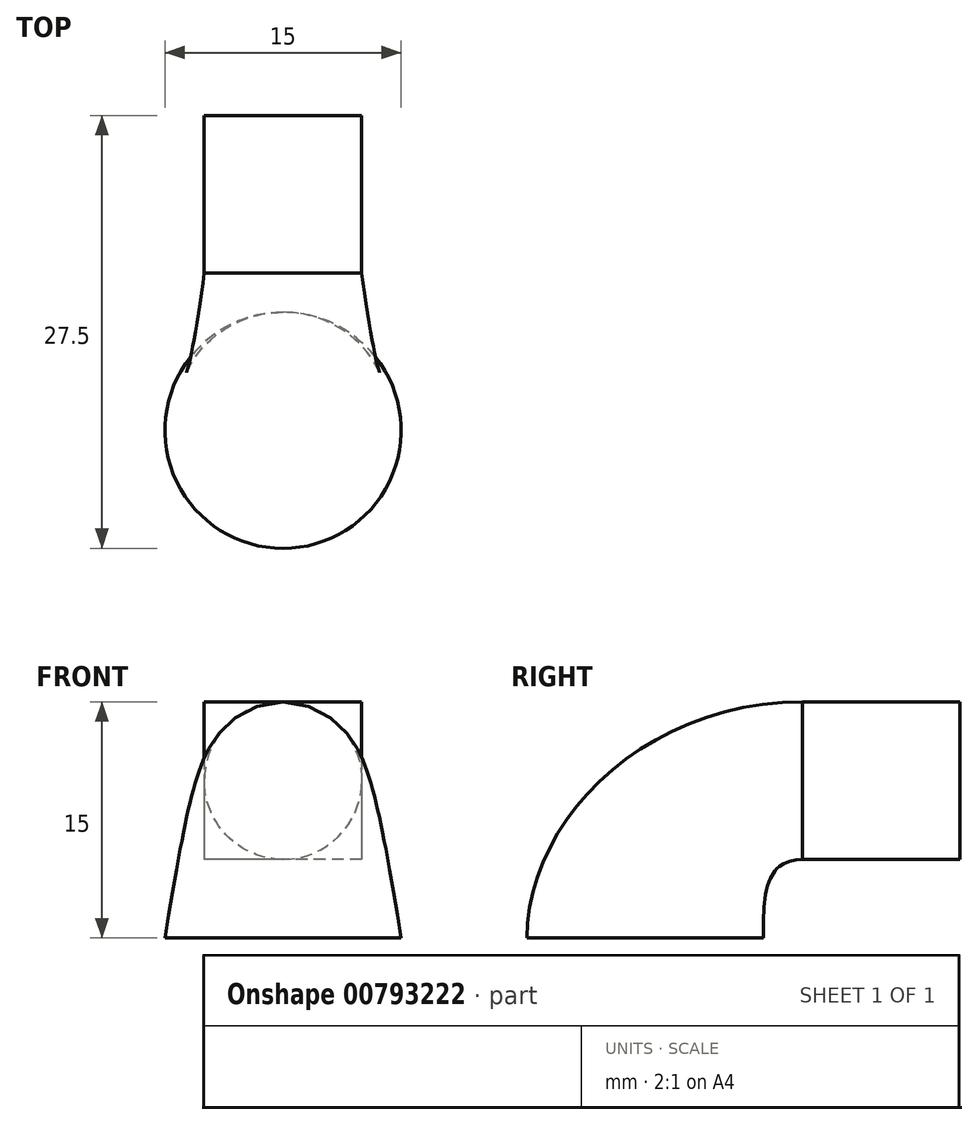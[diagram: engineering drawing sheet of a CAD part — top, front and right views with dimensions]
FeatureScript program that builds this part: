
annotation { "Feature Type Name" : "Feature", "Feature Type Description" : "" }
export const myFeature = defineFeature(function(context is Context, id is Id, definition is map)
    precondition{}
    {
        {
            var Q0;
            Q0=qCreatedBy(makeId("Top.planeOp"),FACE);
            var sketch = newSketch(context, id + "F0", { "sketchPlane" : qUnion([Q0])});
            skPoint(sketch, "E0", {"position": v(0, 0) * mm});
            skLineSegment(sketch, "E1", {"start": v(0, 0) * mm, "end": v(5, 5) * mm, "construction": true});
            skLineSegment(sketch, "E2.bottom", {"start": v(5, 5) * mm, "end": v(-5, 5) * mm});
            skLineSegment(sketch, "E2.top", {"start": v(5, -5) * mm, "end": v(-5, -5) * mm});
            skLineSegment(sketch, "E2.left", {"start": v(5, 5) * mm, "end": v(5, -5) * mm});
            skLineSegment(sketch, "E2.right", {"start": v(-5, 5) * mm, "end": v(-5, -5) * mm});
            skSolve(sketch);
        }
        {
            var Q0;
            Q0=qCreatedBy(makeId("Right.planeOp"),FACE);
            var Q1;
            Q1=sQuery(id+"F0.wireOp",VERTEX,"E1.end");
            cPlane(context, id + "F1", {"entities" : qUnion([Q0, Q1]), "cplaneType" : CPlaneType.PLANE_POINT, "offset" : 0 * mm, "width" : 150 * mm, "height" : 150 * mm});
        }
        {
            var Q0;
            Q0=qCreatedBy(id+"F1.planeOp",FACE);
            var sketch = newSketch(context, id + "F2", { "sketchPlane" : qUnion([Q0])});
            skPoint(sketch, "E3", {"position": v(5, 0) * mm});
            skLineSegment(sketch, "E4", {"start": v(5, 0) * mm, "end": v(5, 10) * mm, "construction": true});
            skSolve(sketch);
        }
        {
            var Q0;
            Q0 = qSketchRegion(id + "F0", true);
            var Q1;
            Q1=sQuery(id+"F2.wireOp",VERTEX,"E4.end");
            extrude(context, id + "F3", {"entities" : qUnion([Q0]), "endBound" : BoundingType.UP_TO_VERTEX, "depth" : 25 * mm, "endBoundEntityVertex" : qUnion([Q1]), "offsetDistance" : 25 * mm});
        }
        {
            var Q0;
            Q0=makeQuery(id+"F3.opExtrude","CAP_FACE",FACE,{"disambiguationData":[OSD([sQuery(id+"F0.wireOp",EDGE,"E2.bottom"),sQuery(id+"F0.wireOp",EDGE,"E2.top"),sQuery(id+"F0.wireOp",EDGE,"E2.left"),sQuery(id+"F0.wireOp",EDGE,"E2.right")])],"isStart":true});
            cPlane(context, id + "F4", {"entities" : qUnion([Q0]), "cplaneType" : CPlaneType.OFFSET, "offset" : 5 * mm, "width" : 150 * mm, "height" : 150 * mm});
        }
        {
            var Q0;
            Q0=makeQuery(id+"F3.opExtrude","SWEPT_FACE",FACE,{"disambiguationData":[OSD([sQuery(id+"F0.wireOp",EDGE,"E2.top")])]});
            var sketch = newSketch(context, id + "F5", { "sketchPlane" : qUnion([Q0])});
            skLineSegment(sketch, "E5", {"start": v(0, 0) * mm, "end": v(0, 5) * mm, "construction": true});
            skCircle(sketch, "E6", {"center": v(0, 5) * mm, "radius": 5 * mm});
            skSolve(sketch);
        }
        {
            var Q0;
            Q0=qCreatedBy(id+"F4.planeOp",FACE);
            var sketch = newSketch(context, id + "F6", { "sketchPlane" : qUnion([Q0])});
            skLineSegment(sketch, "E7", {"start": v(0, 15) * mm, "end": v(0, 5) * mm, "construction": true});
            skCircle(sketch, "E8", {"center": v(0, 15) * mm, "radius": 7.5 * mm});
            skPoint(sketch, "E9", {"position": v(0, 7.5) * mm});
            skPoint(sketch, "E10", {"position": v(0, 22.5) * mm});
            skSolve(sketch);
        }
        {
            var Q0;
            Q0=qCreatedBy(makeId("Right.planeOp"),FACE);
            var Q1;
            Q1=sQuery(id+"F5.wireOp",VERTEX,"E5.end");
            cPlane(context, id + "F7", {"entities" : qUnion([Q0, Q1]), "cplaneType" : CPlaneType.PLANE_POINT, "offset" : 25 * mm, "width" : 150 * mm, "height" : 150 * mm});
        }
        {
            var Q0;
            Q0=qCreatedBy(id+"F7.planeOp",FACE);
            var sketch = newSketch(context, id + "F8", { "sketchPlane" : qUnion([Q0])});
            skLineSegment(sketch, "E11", {"start": v(-5, 0) * mm, "end": v(-4.5, 0) * mm, "construction": true});
            skLineSegment(sketch, "E12", {"start": v(-4.5, 10) * mm, "end": v(-5, 10) * mm, "construction": true});
            skLineSegment(sketch, "E13", {"start": v(-7.5, -5) * mm, "end": v(-7.5, -5.5) * mm, "construction": true});
            skLineSegment(sketch, "E14", {"start": v(-22.5, -5) * mm, "end": v(-22.5, -5.5) * mm, "construction": true});
            skFitSpline(sketch, "E15", {"points": [v(-5, 10) * mm, v(-22.5, -5) * mm], "startDerivative": vector(-30, 0) * mm, "endDerivative": vector(0, -22.5) * mm});
            skFitSpline(sketch, "E16", {"points": [v(-5, 0) * mm, v(-7.5, -5) * mm], "startDerivative": vector(-7.5, 0) * mm, "endDerivative": vector(0, -7.5) * mm});
            skSolve(sketch);
        }
        {
            var Q1;
            {var subQ0=sQuery(id+"F5.wireOp",EDGE,"E6");var subQ1=sQuery(id+"F0.wireOp",EDGE,"E2.top");var subQ2=makeQuery(id+"F5.imprint","INTERSECT",VERTEX,{"derivedFrom":[makeQuery(id+"F3.opExtrude","TWEAK_EDGE",EDGE,{"derivedFrom":[makeQuery(id+"F0.imprint","IMPRINT",EDGE,{"derivedFrom":subQ1}),dummyQuery(id+"F3.vertexPlane.planeOp",FACE)]}),subQ0]});Q1=makeQuery(id+"F5.imprint","IMPRINT",FACE,{"disambiguationData":[TD([[makeQuery(id+"F5.imprint","IMPRINT",EDGE,{"disambiguationData":[TD([[subQ2,1.0]])],"derivedFrom":subQ0}),1.0]])]});}
            var Q2;
            Q2=makeQuery(id+"F6.imprint","IMPRINT",FACE,{"disambiguationData":[TD([[makeQuery(id+"F6.imprint","IMPRINT",EDGE,{"derivedFrom":sQuery(id+"F6.wireOp",EDGE,"E8")}),1.0]])]});
            var Q3;
            Q3=sQuery(id+"F8.wireOp",EDGE,"E15");
            var Q4;
            Q4=sQuery(id+"F8.wireOp",EDGE,"E16");
            loft(context, id + "F9", {"operationType" : NewBodyOperationType.ADD, "addGuides" : true, "sheetProfilesArray" : [{ "sheetProfileEntities" : qUnion([Q1]) }, { "sheetProfileEntities" : qUnion([Q2]) }], "guidesArray" : [{ "guideEntities" : qUnion([Q3]), "guideDerivativeType" : LoftGuideDerivativeType.DEFAULT, "guideDerivativeMagnitude" : 1 }, { "guideEntities" : qUnion([Q4]), "guideDerivativeType" : LoftGuideDerivativeType.DEFAULT, "guideDerivativeMagnitude" : 1 }]});
        }
    });
